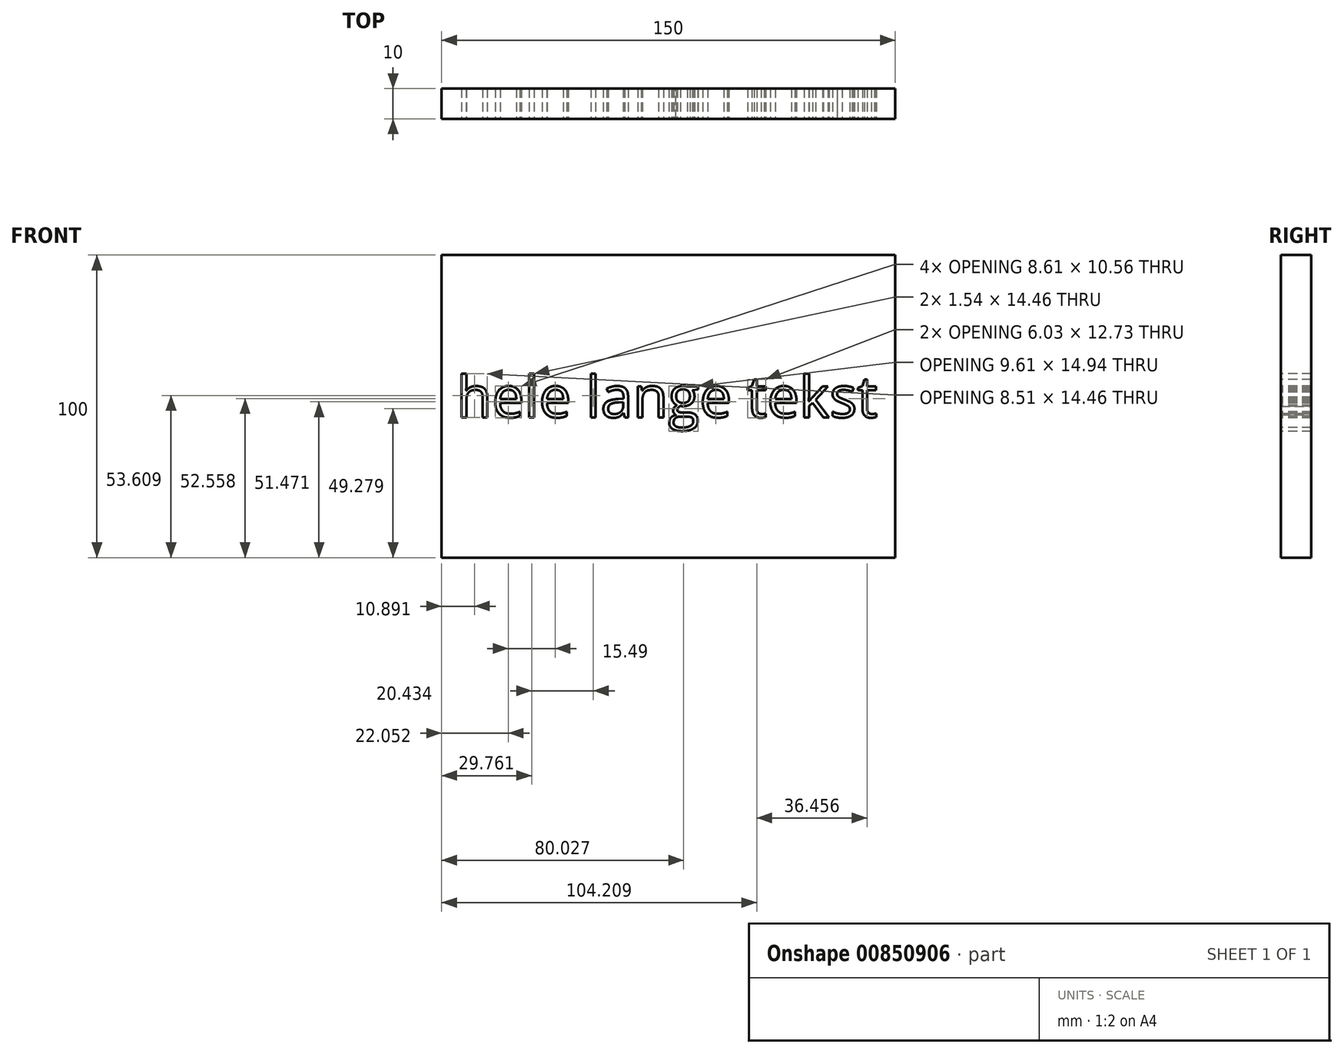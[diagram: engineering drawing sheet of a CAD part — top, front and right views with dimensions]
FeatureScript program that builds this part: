
annotation { "Feature Type Name" : "Feature", "Feature Type Description" : "" }
export const myFeature = defineFeature(function(context is Context, id is Id, definition is map)
    precondition{}
    {
        {
            var Q0;
            Q0=qCreatedBy(makeId("Front.planeOp"),FACE);
            var sketch = newSketch(context, id + "F0", { "sketchPlane" : qUnion([Q0])});
            skLineSegment(sketch, "E0.bottom", {"start": v(-75, 50) * mm, "end": v(75, 50) * mm});
            skLineSegment(sketch, "E0.top", {"start": v(-75, -50) * mm, "end": v(75, -50) * mm});
            skLineSegment(sketch, "E0.left", {"start": v(-75, 50) * mm, "end": v(-75, -50) * mm});
            skLineSegment(sketch, "E0.right", {"start": v(75, 50) * mm, "end": v(75, -50) * mm});
            skPoint(sketch, "E0.middle", {"position": v(0, 0) * mm});
            skSolve(sketch);
        }
        {
            var Q0;
            Q0=makeQuery(id+"F0.imprint","IMPRINT",FACE,{"disambiguationData":[TD([[makeQuery(id+"F0.imprint","IMPRINT",EDGE,{"derivedFrom":sQuery(id+"F0.wireOp",EDGE,"E0.bottom")}),-1.0]])]});
            extrude(context, id + "F1", {"entities" : qUnion([Q0]), "depth" : 10 * mm, "offsetDistance" : 25 * mm});
        }
        {
            var Q0;
            Q0=makeQuery(id+"F1.opExtrude","CAP_FACE",FACE,{"disambiguationData":[OSD([sQuery(id+"F0.wireOp",EDGE,"E0.bottom"),sQuery(id+"F0.wireOp",EDGE,"E0.top"),sQuery(id+"F0.wireOp",EDGE,"E0.left"),sQuery(id+"F0.wireOp",EDGE,"E0.right")])],"isStart":false});
            var sketch = newSketch(context, id + "F2", { "sketchPlane" : qUnion([Q0])});
            skText(sketch, "E1", { "text": "hele lange tekst", "fontName": "OpenSans-Regular.ttf"});
            const initialGuessF2  = {"E1": [-0.07, -0.00362, 1, 0, 0.0137]};
            skSetInitialGuess(sketch, initialGuessF2);
            skSolve(sketch);
        }
        {
            var Q0;
            Q0 = qSketchRegion(id + "F2", true);
            extrude(context, id + "F3", {"entities" : qUnion([Q0]), "operationType" : NewBodyOperationType.REMOVE, "endBound" : BoundingType.THROUGH_ALL, "oppositeDirection" : true, "depth" : 25 * mm, "offsetDistance" : 25 * mm});
        }
    });
